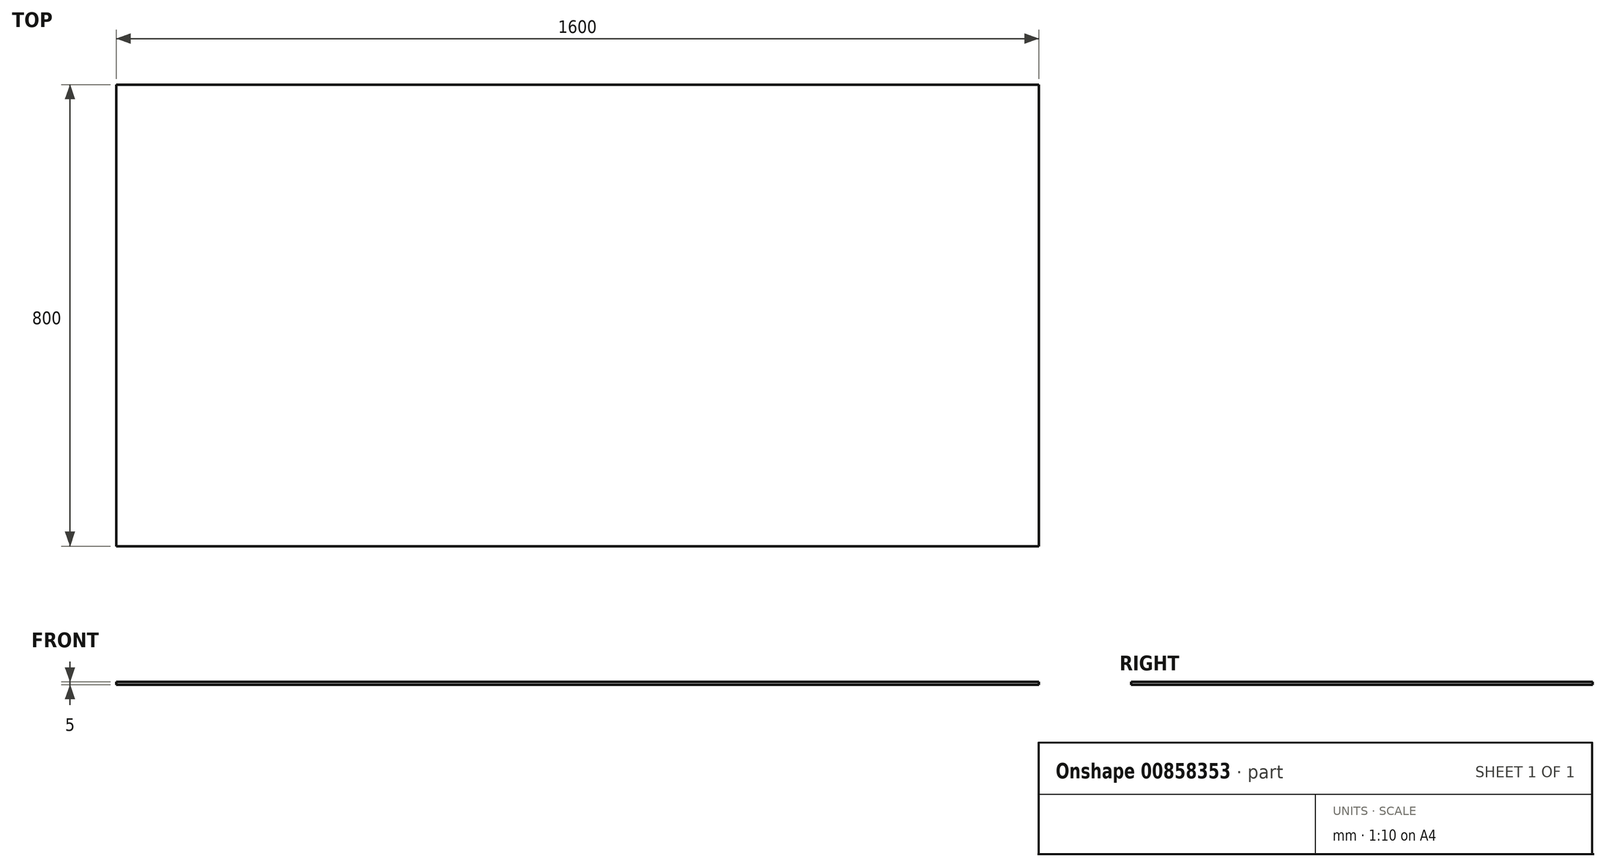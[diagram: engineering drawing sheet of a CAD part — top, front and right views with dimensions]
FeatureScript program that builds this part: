
annotation { "Feature Type Name" : "Feature", "Feature Type Description" : "" }
export const myFeature = defineFeature(function(context is Context, id is Id, definition is map)
    precondition{}
    {
        {
            var Q0;
            Q0=qCreatedBy(makeId("Top.planeOp"),FACE);
            var sketch = newSketch(context, id + "F0", { "sketchPlane" : qUnion([Q0])});
            skLineSegment(sketch, "E0.bottom", {"start": v(800, 400) * mm, "end": v(-800, 400) * mm});
            skLineSegment(sketch, "E0.top", {"start": v(800, -400) * mm, "end": v(-800, -400) * mm});
            skLineSegment(sketch, "E0.left", {"start": v(800, 400) * mm, "end": v(800, -400) * mm});
            skLineSegment(sketch, "E0.right", {"start": v(-800, 400) * mm, "end": v(-800, -400) * mm});
            skPoint(sketch, "E0.middle", {"position": v(0, 0) * mm});
            skSolve(sketch);
        }
        {
            var Q0;
            Q0=makeQuery(id+"F0.imprint","IMPRINT",FACE,{"disambiguationData":[TD([[makeQuery(id+"F0.imprint","IMPRINT",EDGE,{"derivedFrom":sQuery(id+"F0.wireOp",EDGE,"E0.bottom")}),1.0]])]});
            extrude(context, id + "F1", {"entities" : qUnion([Q0]), "oppositeDirection" : true, "depth" : 5 * mm, "offsetDistance" : 25 * mm});
        }
    });
